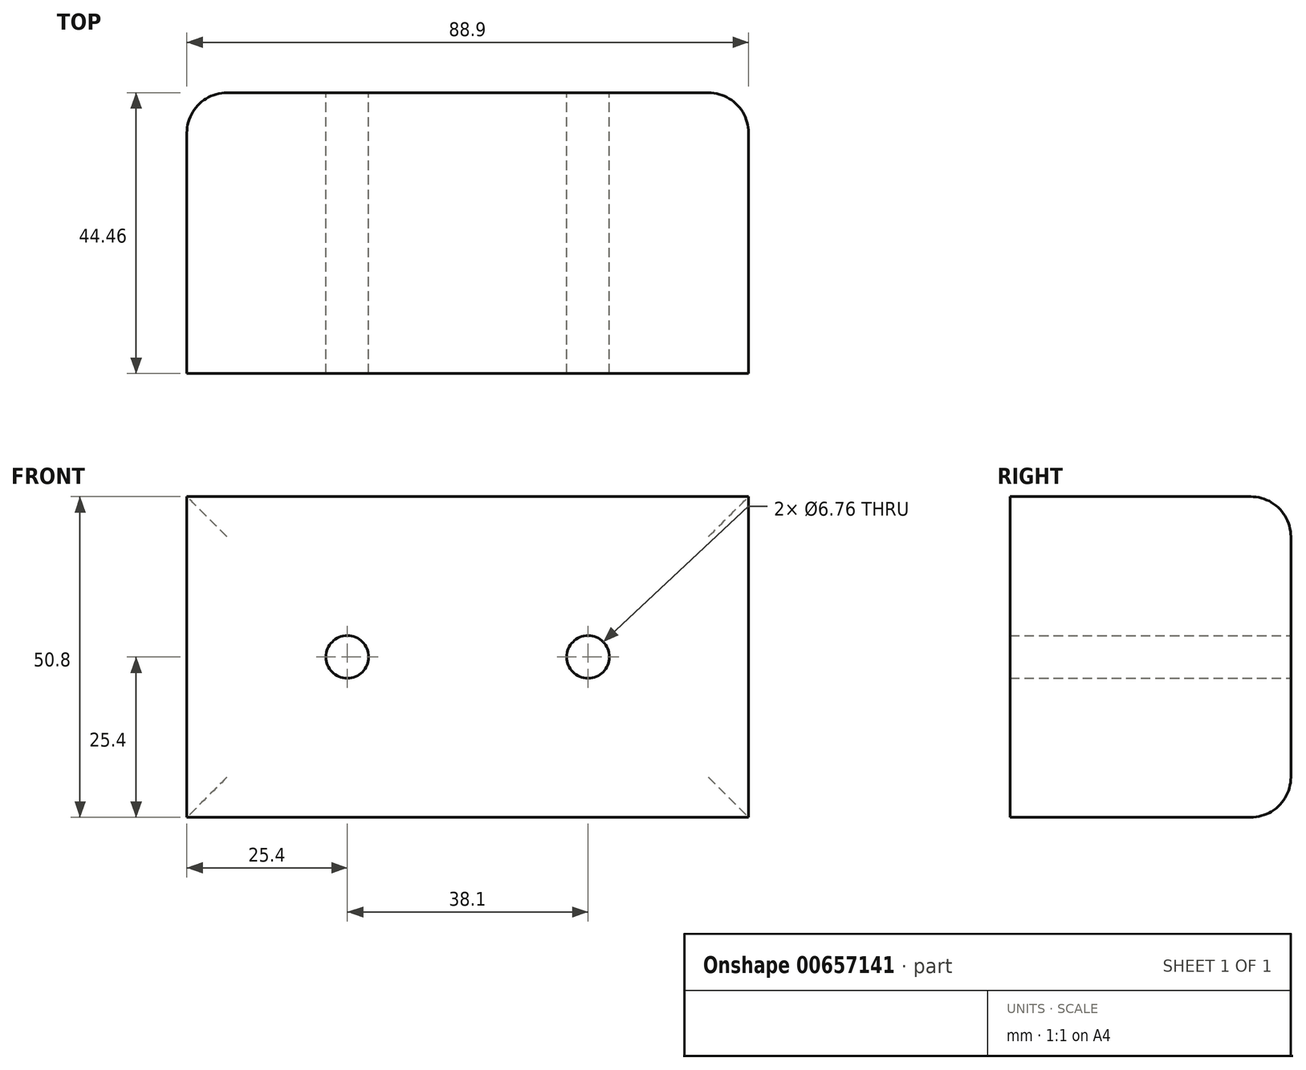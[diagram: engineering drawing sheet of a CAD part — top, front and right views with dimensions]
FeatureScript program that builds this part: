
annotation { "Feature Type Name" : "Feature", "Feature Type Description" : "" }
export const myFeature = defineFeature(function(context is Context, id is Id, definition is map)
    precondition{}
    {
        {
            var Q0;
            Q0=qCreatedBy(makeId("Top.planeOp"),FACE);
            var sketch = newSketch(context, id + "F0", { "sketchPlane" : qUnion([Q0])});
            skLineSegment(sketch, "E0.bottom", {"start": v(44.45, -22.22) * mm, "end": v(-44.45, -22.23) * mm});
            skLineSegment(sketch, "E0.top", {"start": v(44.45, 22.23) * mm, "end": v(-44.45, 22.22) * mm});
            skLineSegment(sketch, "E0.left", {"start": v(44.45, -22.22) * mm, "end": v(44.45, 22.23) * mm});
            skLineSegment(sketch, "E0.right", {"start": v(-44.45, -22.23) * mm, "end": v(-44.45, 22.23) * mm});
            skPoint(sketch, "E0.middle", {"position": v(0, 0) * mm});
            skSolve(sketch);
        }
        {
            var Q0;
            Q0=makeQuery(id+"F0.imprint","IMPRINT",FACE,{"disambiguationData":[TD([[makeQuery(id+"F0.imprint","IMPRINT",EDGE,{"derivedFrom":sQuery(id+"F0.wireOp",EDGE,"E0.bottom")}),-1.0]])]});
            extrude(context, id + "F1", {"entities" : qUnion([Q0]), "depth" : 50.8 * mm, "offsetDistance" : 25.4 * mm});
        }
        {
            var Q0;
            Q0=makeQuery(id+"F1.opExtrude","SWEPT_FACE",FACE,{"disambiguationData":[OSD([sQuery(id+"F0.wireOp",EDGE,"E0.top")])]});
            var sketch = newSketch(context, id + "F2", { "sketchPlane" : qUnion([Q0])});
            skPoint(sketch, "E1", {"position": v(19.05, 25.4) * mm});
            skPoint(sketch, "E2", {"position": v(-19.05, 25.4) * mm});
            skLineSegment(sketch, "E3", {"start": v(44.45, 25.4) * mm, "end": v(-44.45, 25.4) * mm, "construction": true});
            skLineSegment(sketch, "E4", {"start": v(0, 0) * mm, "end": v(0, 50.8) * mm, "construction": true});
            skSolve(sketch);
        }
        {
            var Q0;
            Q0=sQuery(id+"F2.wireOp",VERTEX,"E2");
            var Q1;
            Q1=sQuery(id+"F2.wireOp",VERTEX,"E1");
            var Q2;
            Q2=makeQuery(id+"F1.opExtrude","SWEPT_BODY",BODY,{"disambiguationData":[OSD([sQuery(id+"F0.wireOp",EDGE,"E0.bottom"),sQuery(id+"F0.wireOp",EDGE,"E0.top"),sQuery(id+"F0.wireOp",EDGE,"E0.left"),sQuery(id+"F0.wireOp",EDGE,"E0.right")])]});
            hole(context, id + "F3", {"style" : HoleStyle.SIMPLE, "endStyle" : HoleEndStyle.THROUGH, "standardTappedOrClearance" : lookupTablePath({ "standard" : "ANSI", "fit" : "Normal (ASME)", "size" : "1/4", "type" : "Clearance" }), "standardBlindInLast" : lookupTablePath({ "fit" : "Free", "standard" : "ANSI", "size" : "1/4", "type" : "Clearance" }), "holeDiameter" : 6.76 * mm, "majorDiameter" : 6.35 * mm, "isTappedThrough" : true, "tappedDepth" : 12.7 * mm, "tapClearance" : 3, "locations" : qUnion([Q0, Q1]), "scope" : qUnion([Q2])});
        }
        {
            var Q0;
            Q0=makeQuery(id+"F1.opExtrude","CAP_EDGE",EDGE,{"disambiguationData":[OSD([sQuery(id+"F0.wireOp",EDGE,"E0.top")])],"isStart":false});
            var Q1;
            Q1=makeQuery(id+"F1.opExtrude","SWEPT_EDGE",EDGE,{"disambiguationData":[OSD([sQuery(id+"F0.wireOp",EDGE,"E0.top"),sQuery(id+"F0.wireOp",EDGE,"E0.right")])]});
            var Q2;
            Q2=makeQuery(id+"F1.opExtrude","CAP_EDGE",EDGE,{"disambiguationData":[OSD([sQuery(id+"F0.wireOp",EDGE,"E0.top")])],"isStart":true});
            var Q3;
            Q3=makeQuery(id+"F1.opExtrude","SWEPT_EDGE",EDGE,{"disambiguationData":[OSD([sQuery(id+"F0.wireOp",EDGE,"E0.top"),sQuery(id+"F0.wireOp",EDGE,"E0.left")])]});
            fillet(context, id + "F4", {"entities" : qUnion([Q0, Q1, Q2, Q3]), "radius" : 6.35 * mm, "tangentPropagation" : true, "allowEdgeOverflow" : false});
        }
    });
